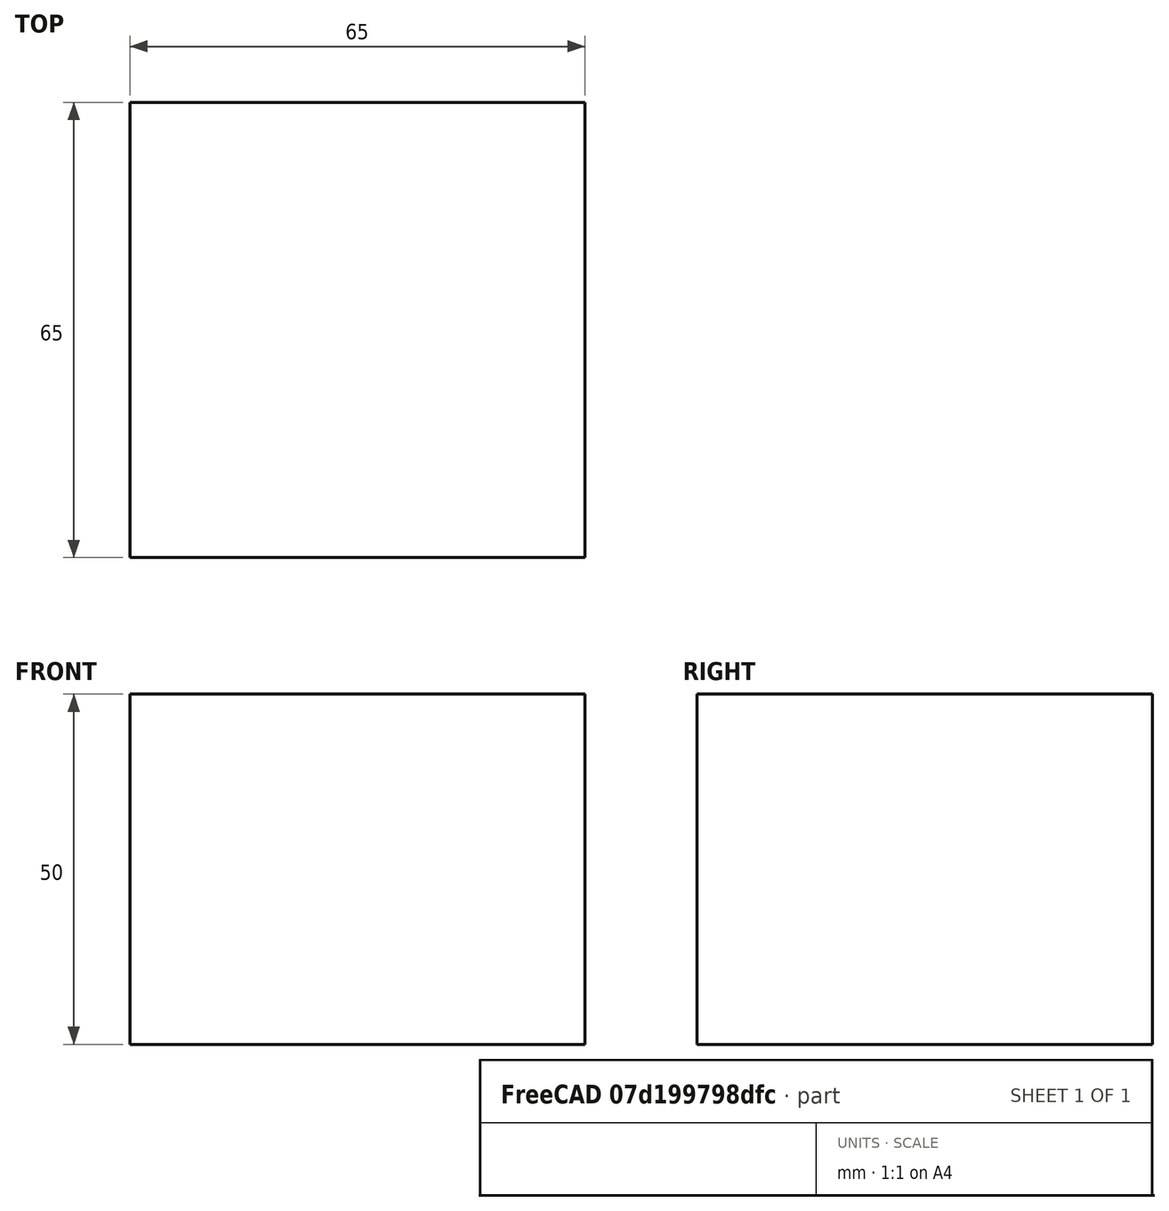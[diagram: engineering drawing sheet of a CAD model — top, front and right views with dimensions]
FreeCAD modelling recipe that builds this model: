
FCSTD DOCUMENT  (FreeCAD 0.15R4671 (Git))
Label: Square Bar 65 EN10059 S235JR
License: All rights reserved
LicenseURL: http://en.wikipedia.org/wiki/All_rights_reserved
objects: Sketcher::SketchObject×1, Part::Extrusion×1
note: 2 computed .brp shape members not serialized (recipe doc carries the construction recipe); baked Part::Feature solids carry a one-line shape summary decoded from their .brp

FEATURE [Sketcher::SketchObject] Sketch
  sketch-geometry (4):
    g0: LineSegment StartX=-32.5 StartY=-32.5 StartZ=0 EndX=32.5 EndY=-32.5 EndZ=0
    g1: LineSegment StartX=32.5 StartY=-32.5 StartZ=0 EndX=32.5 EndY=32.5 EndZ=0
    g2: LineSegment StartX=32.5 StartY=32.5 StartZ=0 EndX=-32.5 EndY=32.5 EndZ=0
    g3: LineSegment StartX=-32.5 StartY=32.5 StartZ=0 EndX=-32.5 EndY=-32.5 EndZ=0
  constraints (12):
    c: Coincident(g0,g1)
    c: Coincident(g1,g2)
    c: Coincident(g2,g3)
    c: Coincident(g3,g0)
    c: Horizontal(g0)
    c: Horizontal(g2)
    c: Vertical(g1)
    c: Vertical(g3)
    c: Symmetric(g1,g0,g-1)
    c: Symmetric(g2,g1,g-2)
    c: Equal(g1,g2)
    c: DistanceY(g1) = 65
FEATURE [Part::Extrusion] Extrude  label="Square Bar 65 EN10059 S235JR"
  Base = -> Sketch
  Dir = (0,0,50)
  Solid = true
